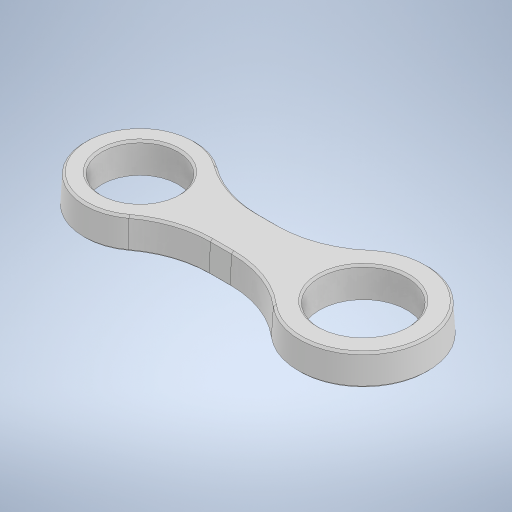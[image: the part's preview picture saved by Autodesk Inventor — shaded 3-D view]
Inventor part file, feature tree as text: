
AUTODESK INVENTOR PART (.ipt)
format: ipt  version: 2023 (Build 270158000, 158)  size: 317,440 bytes
history: native  units: in
note: dims shown in document units (in); Inventor stores cm internally (conversion verified against a paired STEP export)
features: chamfer x2, extrude x1, fillet x1, draft x1, sketch x1
ambient origin geometry x8: Origin, YZ Plane, XZ Plane, XY Plane, X Axis, Y Axis, Z Axis, Center Point
bodies: Body1 (feature_tree)
feature tree (6):
  extrude  "Extrusion2"  Depth=1.0in
  fillet  "Fillet3"  Radius=1.3in
  draft  "FaceDraft2"
  chamfer  "Chamfer1"  Distance=0.76in
  chamfer  "Chamfer2"  Distance=1.125in
  sketch  "Sketch1"  dims[d15=0.872in d17=0.5in d18=1.3in d19=0.76in d20=1.125in d21=2.225in d22=0.3in d23=0.0in d27=1.0in d28=0.0206in d29=0.02in d30=0.125in d31=45.0deg d32=0.02in d33=0.125in d34=45.0deg d3=0.5in d4=0.0344in d5=0.5in d6=0.0344in]
